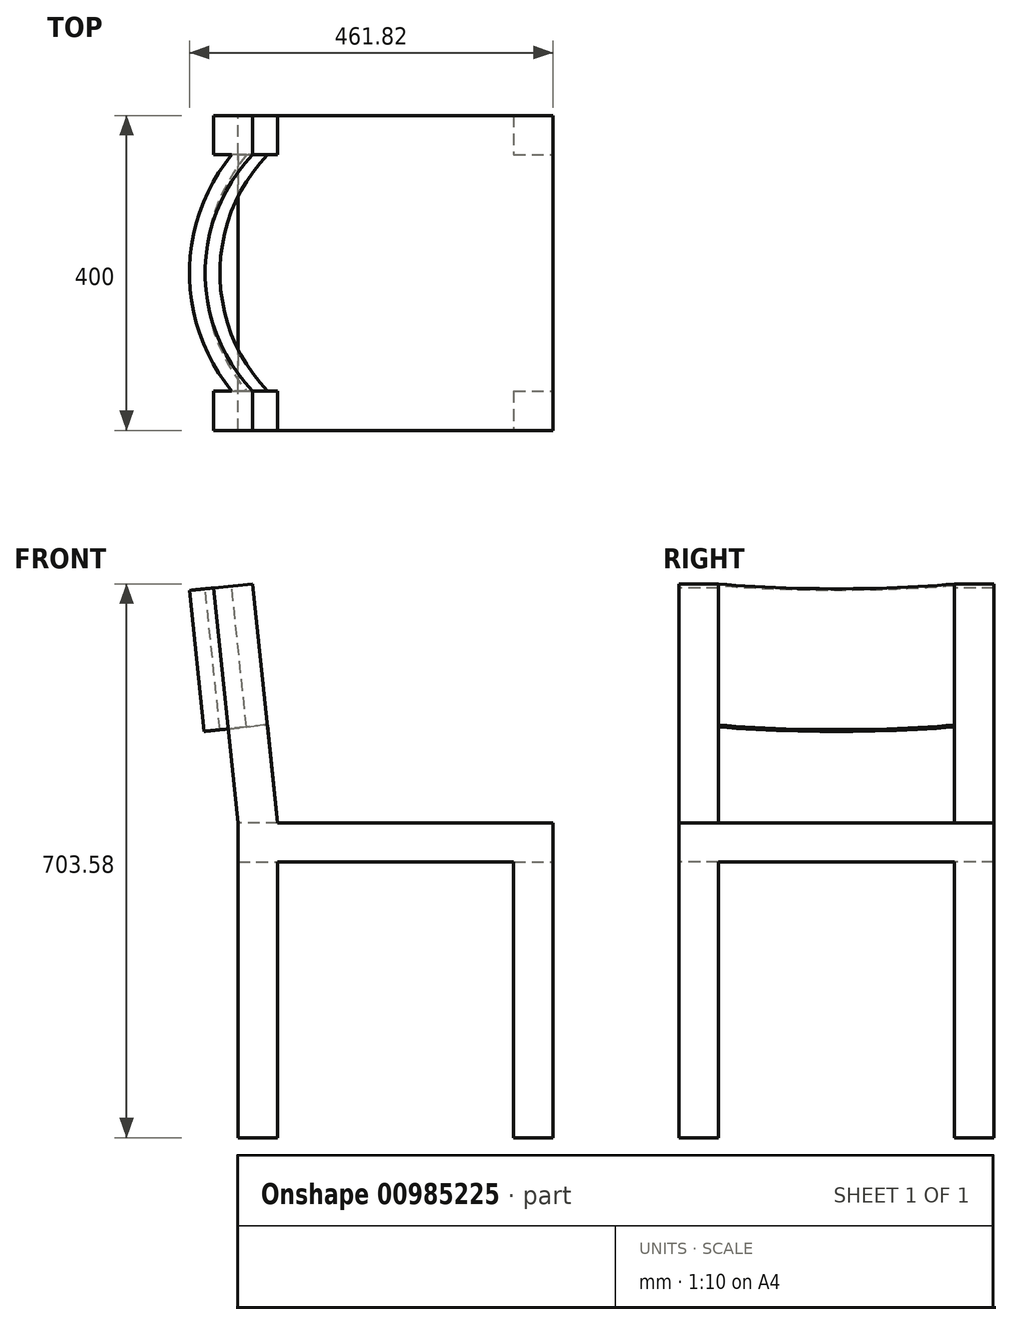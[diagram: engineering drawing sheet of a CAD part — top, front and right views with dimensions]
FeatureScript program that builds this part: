
annotation { "Feature Type Name" : "Feature", "Feature Type Description" : "" }
export const myFeature = defineFeature(function(context is Context, id is Id, definition is map)
    precondition{}
    {
        {
            var Q0;
            Q0=qCreatedBy(makeId("Top.planeOp"),FACE);
            var sketch = newSketch(context, id + "F0", { "sketchPlane" : qUnion([Q0])});
            skLineSegment(sketch, "E0.bottom", {"start": v(200, -200) * mm, "end": v(-200, -200) * mm});
            skLineSegment(sketch, "E0.top", {"start": v(200, 200) * mm, "end": v(-200, 200) * mm});
            skLineSegment(sketch, "E0.left", {"start": v(200, -200) * mm, "end": v(200, 200) * mm});
            skLineSegment(sketch, "E0.right", {"start": v(-200, -200) * mm, "end": v(-200, 200) * mm});
            skPoint(sketch, "E0.middle", {"position": v(0, 0) * mm});
            skSolve(sketch);
        }
        {
            var Q0;
            Q0=makeQuery(id+"F0.imprint","IMPRINT",FACE,{"disambiguationData":[TD([[makeQuery(id+"F0.imprint","IMPRINT",EDGE,{"derivedFrom":sQuery(id+"F0.wireOp",EDGE,"E0.bottom")}),-1.0]])]});
            extrude(context, id + "F1", {"entities" : qUnion([Q0]), "depth" : 400 * mm, "offsetDistance" : 25 * mm});
        }
        {
            var Q0;
            Q0=makeQuery(id+"F1.opExtrude","SWEPT_FACE",FACE,{"disambiguationData":[OSD([sQuery(id+"F0.wireOp",EDGE,"E0.bottom")])]});
            var sketch = newSketch(context, id + "F2", { "sketchPlane" : qUnion([Q0])});
            skLineSegment(sketch, "E1", {"start": v(200, 0) * mm, "end": v(150, 0) * mm});
            skLineSegment(sketch, "E2", {"start": v(150, 0) * mm, "end": v(150, 350) * mm});
            skLineSegment(sketch, "E3", {"start": v(150, 350) * mm, "end": v(-150, 350) * mm});
            skLineSegment(sketch, "E4", {"start": v(-150, 350) * mm, "end": v(-150, 0) * mm});
            skSolve(sketch);
        }
        {
            var Q0;
            {var subQ0=sQuery(id+"F2.wireOp",EDGE,"E2");Q0=makeQuery(id+"F2.imprint","IMPRINT",FACE,{"disambiguationData":[TD([[makeQuery(id+"F2.imprint","IMPRINT",EDGE,{"derivedFrom":subQ0}),1.0]])]});}
            extrude(context, id + "F3", {"entities" : qUnion([Q0]), "operationType" : NewBodyOperationType.REMOVE, "endBound" : BoundingType.THROUGH_ALL, "oppositeDirection" : true, "depth" : 25 * mm, "offsetDistance" : 25 * mm});
        }
        {
            var Q0;
            Q0=makeQuery(id+"F1.opExtrude","SWEPT_FACE",FACE,{"disambiguationData":[OSD([sQuery(id+"F0.wireOp",EDGE,"E0.left")])]});
            var sketch = newSketch(context, id + "F4", { "sketchPlane" : qUnion([Q0])});
            skLineSegment(sketch, "E5", {"start": v(-200, 0) * mm, "end": v(-150, 0) * mm});
            skLineSegment(sketch, "E6", {"start": v(-150, 0) * mm, "end": v(-150, 350) * mm});
            skLineSegment(sketch, "E7", {"start": v(-150, 350) * mm, "end": v(150, 350) * mm});
            skLineSegment(sketch, "E8", {"start": v(150, 350) * mm, "end": v(150, 0) * mm});
            skSolve(sketch);
        }
        {
            var Q0;
            {var subQ0=sQuery(id+"F4.wireOp",EDGE,"E6");Q0=makeQuery(id+"F4.imprint","IMPRINT",FACE,{"disambiguationData":[TD([[makeQuery(id+"F4.imprint","IMPRINT",EDGE,{"derivedFrom":subQ0}),-1.0]])]});}
            extrude(context, id + "F5", {"entities" : qUnion([Q0]), "operationType" : NewBodyOperationType.REMOVE, "endBound" : BoundingType.THROUGH_ALL, "oppositeDirection" : true, "depth" : 25 * mm, "offsetDistance" : 25 * mm});
        }
        {
            var Q0;
            Q0=makeQuery(id+"F1.opExtrude","CAP_FACE",FACE,{"disambiguationData":[OSD([sQuery(id+"F0.wireOp",EDGE,"E0.bottom"),sQuery(id+"F0.wireOp",EDGE,"E0.top"),sQuery(id+"F0.wireOp",EDGE,"E0.left"),sQuery(id+"F0.wireOp",EDGE,"E0.right")])],"isStart":false});
            var Q1;
            Q1=makeQuery(id+"F1.opExtrude","CAP_VERTEX",VERTEX,{"disambiguationData":[OSD([sQuery(id+"F0.wireOp",EDGE,"E0.top"),sQuery(id+"F0.wireOp",EDGE,"E0.right")])],"isStart":false});
            cPlane(context, id + "F6", {"entities" : qUnion([Q0, Q1]), "cplaneType" : CPlaneType.PLANE_POINT, "offset" : 25 * mm, "width" : 150 * mm, "height" : 150 * mm});
        }
        {
            var Q0;
            Q0=makeQuery(id+"F1.opExtrude","SWEPT_FACE",FACE,{"disambiguationData":[OSD([sQuery(id+"F0.wireOp",EDGE,"E0.right")])]});
            var Q1;
            Q1=makeQuery(id+"F1.opExtrude","CAP_VERTEX",VERTEX,{"disambiguationData":[OSD([sQuery(id+"F0.wireOp",EDGE,"E0.top"),sQuery(id+"F0.wireOp",EDGE,"E0.right")])],"isStart":false});
            cPlane(context, id + "F7", {"entities" : qUnion([Q0, Q1]), "cplaneType" : CPlaneType.PLANE_POINT, "offset" : 25 * mm, "width" : 150 * mm, "height" : 150 * mm});
        }
        {
            var Q0;
            Q0=qCreatedBy(id+"F7.planeOp",FACE);
            var sketch = newSketch(context, id + "F8", { "sketchPlane" : qUnion([Q0])});
            skLineSegment(sketch, "E9", {"start": v(-200, 400) * mm, "end": v(200, 400) * mm, "construction": true});
            skSolve(sketch);
        }
        {
            var Q0;
            Q0=sQuery(id+"F8.wireOp",EDGE,"E9");
            cPlane(context, id + "F9", {"entities" : qUnion([Q0]), "cplaneType" : CPlaneType.LINE_ANGLE, "offset" : 25 * mm, "angle" : 84 * degree, "oppositeDirection" : true, "width" : 150 * mm, "height" : 150 * mm});
        }
        {
            var Q0;
            Q0=qCreatedBy(id+"F9.planeOp",FACE);
            var sketch = newSketch(context, id + "F10", { "sketchPlane" : qUnion([Q0])});
            skLineSegment(sketch, "E10.bottom", {"start": v(-200, 418.71) * mm, "end": v(200, 418.71) * mm});
            skLineSegment(sketch, "E10.top", {"start": v(-200, 718.71) * mm, "end": v(200, 718.71) * mm});
            skLineSegment(sketch, "E10.left", {"start": v(-200, 418.71) * mm, "end": v(-200, 718.71) * mm});
            skLineSegment(sketch, "E10.right", {"start": v(200, 418.71) * mm, "end": v(200, 718.71) * mm});
            skSolve(sketch);
        }
        {
            var Q0;
            Q0=makeQuery(id+"F10.imprint","IMPRINT",FACE,{"disambiguationData":[TD([[makeQuery(id+"F10.imprint","IMPRINT",EDGE,{"derivedFrom":sQuery(id+"F10.wireOp",EDGE,"E10.bottom")}),1.0]])]});
            extrude(context, id + "F11", {"entities" : qUnion([Q0]), "oppositeDirection" : true, "depth" : 50 * mm, "offsetDistance" : 25 * mm});
        }
        {
            var Q0;
            Q0=makeQuery(id+"F11.opExtrude","CAP_FACE",FACE,{"disambiguationData":[OSD([sQuery(id+"F10.wireOp",EDGE,"E10.bottom"),sQuery(id+"F10.wireOp",EDGE,"E10.top"),sQuery(id+"F10.wireOp",EDGE,"E10.left"),sQuery(id+"F10.wireOp",EDGE,"E10.right")])],"isStart":false});
            var sketch = newSketch(context, id + "F12", { "sketchPlane" : qUnion([Q0])});
            skLineSegment(sketch, "E11", {"start": v(-200, 418.71) * mm, "end": v(-150, 418.71) * mm});
            skLineSegment(sketch, "E12", {"start": v(-150, 418.71) * mm, "end": v(-150, 718.71) * mm});
            skLineSegment(sketch, "E13", {"start": v(-150, 718.71) * mm, "end": v(150, 718.71) * mm});
            skLineSegment(sketch, "E14", {"start": v(150, 718.71) * mm, "end": v(150, 418.71) * mm});
            skSolve(sketch);
        }
        {
            var Q0;
            {var subQ0=sQuery(id+"F12.wireOp",EDGE,"E12");Q0=makeQuery(id+"F12.imprint","IMPRINT",FACE,{"disambiguationData":[TD([[makeQuery(id+"F12.imprint","IMPRINT",EDGE,{"derivedFrom":subQ0}),-1.0]])]});}
            extrude(context, id + "F13", {"entities" : qUnion([Q0]), "operationType" : NewBodyOperationType.REMOVE, "endBound" : BoundingType.THROUGH_ALL, "oppositeDirection" : true, "depth" : 25 * mm, "offsetDistance" : 25 * mm});
        }
        {
            var Q0;
            Q0=makeQuery(id+"F1.opExtrude","SWEPT_FACE",FACE,{"disambiguationData":[OSD([sQuery(id+"F0.wireOp",EDGE,"E0.top")])]});
            var sketch = newSketch(context, id + "F14", { "sketchPlane" : qUnion([Q0])});
            skLineSegment(sketch, "E15", {"start": v(200, 400) * mm, "end": v(149.72, 400) * mm});
            skLineSegment(sketch, "E16", {"start": v(150.27, 405.23) * mm, "end": v(200, 400) * mm});
            skLineSegment(sketch, "E17", {"start": v(150.27, 405.23) * mm, "end": v(149.72, 400) * mm});
            skSolve(sketch);
        }
        {
            var Q0;
            Q0=makeQuery(id+"F14.imprint","IMPRINT",FACE,{"disambiguationData":[TD([[makeQuery(id+"F14.imprint","IMPRINT",EDGE,{"derivedFrom":sQuery(id+"F14.wireOp",EDGE,"E15")}),1.0]])]});
            extrude(context, id + "F15", {"entities" : qUnion([Q0]), "operationType" : NewBodyOperationType.ADD, "oppositeDirection" : true, "depth" : 50 * mm, "offsetDistance" : 25 * mm});
        }
        {
            var Q0;
            Q0=makeQuery(id+"F1.opExtrude","SWEPT_FACE",FACE,{"disambiguationData":[OSD([sQuery(id+"F0.wireOp",EDGE,"E0.bottom")])]});
            var sketch = newSketch(context, id + "F16", { "sketchPlane" : qUnion([Q0])});
            skLineSegment(sketch, "E18", {"start": v(-200, 400) * mm, "end": v(-150.27, 405.23) * mm});
            skLineSegment(sketch, "E19", {"start": v(-149.72, 400) * mm, "end": v(-200, 400) * mm});
            skLineSegment(sketch, "E20", {"start": v(-150.27, 405.23) * mm, "end": v(-149.72, 400) * mm});
            skSolve(sketch);
        }
        {
            var Q0;
            Q0=makeQuery(id+"F16.imprint","IMPRINT",FACE,{"disambiguationData":[TD([[makeQuery(id+"F16.imprint","IMPRINT",EDGE,{"derivedFrom":sQuery(id+"F16.wireOp",EDGE,"E18")}),-1.0]])]});
            extrude(context, id + "F17", {"entities" : qUnion([Q0]), "operationType" : NewBodyOperationType.ADD, "oppositeDirection" : true, "depth" : 50 * mm, "offsetDistance" : 25 * mm});
        }
        {
            var Q0;
            {var subQ1=sQuery(id+"F10.wireOp",EDGE,"E10.left");var subQ2=sQuery(id+"F10.wireOp",EDGE,"E10.top");Q0=makeQuery(id+"F13.boolean.opBoolean","SPLIT",FACE,{"disambiguationData":[TD([makeQuery(id+"F11.opExtrude","SWEPT_FACE",FACE,{"disambiguationData":[OSD([subQ1])]})])],"derivedFrom":makeQuery(id+"F11.opExtrude","SWEPT_FACE",FACE,{"disambiguationData":[OSD([subQ2])]})});}
            var sketch = newSketch(context, id + "F18", { "sketchPlane" : qUnion([Q0])});
            skArc(sketch, "E21", {"start": v(-107.1, 150) * mm, "mid": v(-167.72, 0) * mm, "end": v(-107.1, -150) * mm});
            skArc(sketch, "E22.0", {"start": v(-133.88, 150) * mm, "mid": v(-187.72, 0) * mm, "end": v(-133.88, -150) * mm});
            skLineSegment(sketch, "E23", {"start": v(-133.88, -150) * mm, "end": v(-107.1, -150) * mm});
            skLineSegment(sketch, "E24", {"start": v(-133.88, 150) * mm, "end": v(-107.1, 150) * mm});
            skSolve(sketch);
        }
        {
            var Q0;
            Q0=makeQuery(id+"F18.imprint","IMPRINT",FACE,{"disambiguationData":[TD([[makeQuery(id+"F18.imprint","IMPRINT",EDGE,{"derivedFrom":sQuery(id+"F18.wireOp",EDGE,"E21")}),-1.0]])]});
            extrude(context, id + "F19", {"entities" : qUnion([Q0]), "operationType" : NewBodyOperationType.ADD, "oppositeDirection" : true, "depth" : 180 * mm, "offsetDistance" : 25 * mm});
        }
    });
